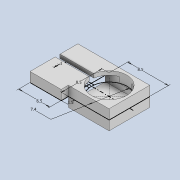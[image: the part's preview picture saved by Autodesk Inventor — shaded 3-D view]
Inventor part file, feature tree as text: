
AUTODESK INVENTOR PART (.ipt)
format: ipt  version: 2020 (Build 240168000, 168)  size: 121,344 bytes
history: native  units: mm
features: extrude x3, sketch x1, shell x1
ambient origin geometry x8: Origin, YZ Plane, XZ Plane, XY Plane, X Axis, Y Axis, Z Axis, Center Point
bodies: Solid1 (feature_tree)
feature tree (5):
  sketch  "Sketch1"  dims[d0=8.5mm d1=8.5mm d2=7.4mm d3=4.0mm d4=0.0mm d6=1.0mm d7=4.0mm d8=0.0mm d9=1.5mm d10=6.5mm d11=0.8mm d12=10.0mm d13=0.0mm d14=0.5mm d15=0.872665mm]
  extrude  "Extrusion1"  Depth=8.5mm
  shell  "Shell2"  Thickness=7.4mm
  extrude  "Extrusion2"  Depth=4.0mm TaperAngle=0.0deg
  extrude  "Extrusion3"  Depth=1.0mm
